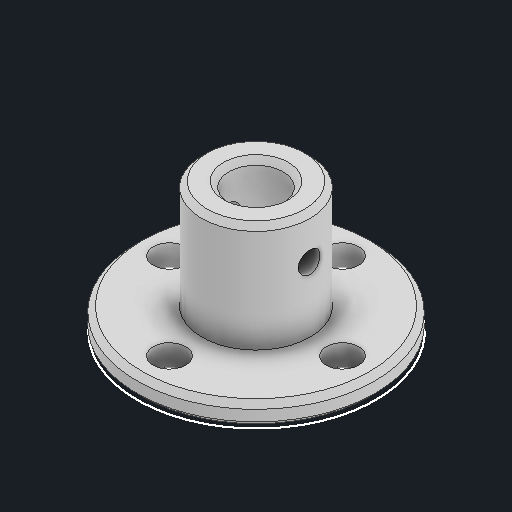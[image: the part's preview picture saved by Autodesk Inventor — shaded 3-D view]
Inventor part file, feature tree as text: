
AUTODESK INVENTOR PART (.ipt)
format: ipt  version: 2023 (Build 270158000, 158)  size: 155,136 bytes
history: native  units: mm
features: other x1, sketch x1
ambient origin geometry x8: Origin, YZ Plane, XZ Plane, XY Plane, X Axis, Y Axis, Z Axis, Center Point
bodies: Solid2 (feature_tree), Solid1 (feature_tree)
feature tree (2):
  other  "Repaired Geometry1"
  sketch  "Sketch1"
